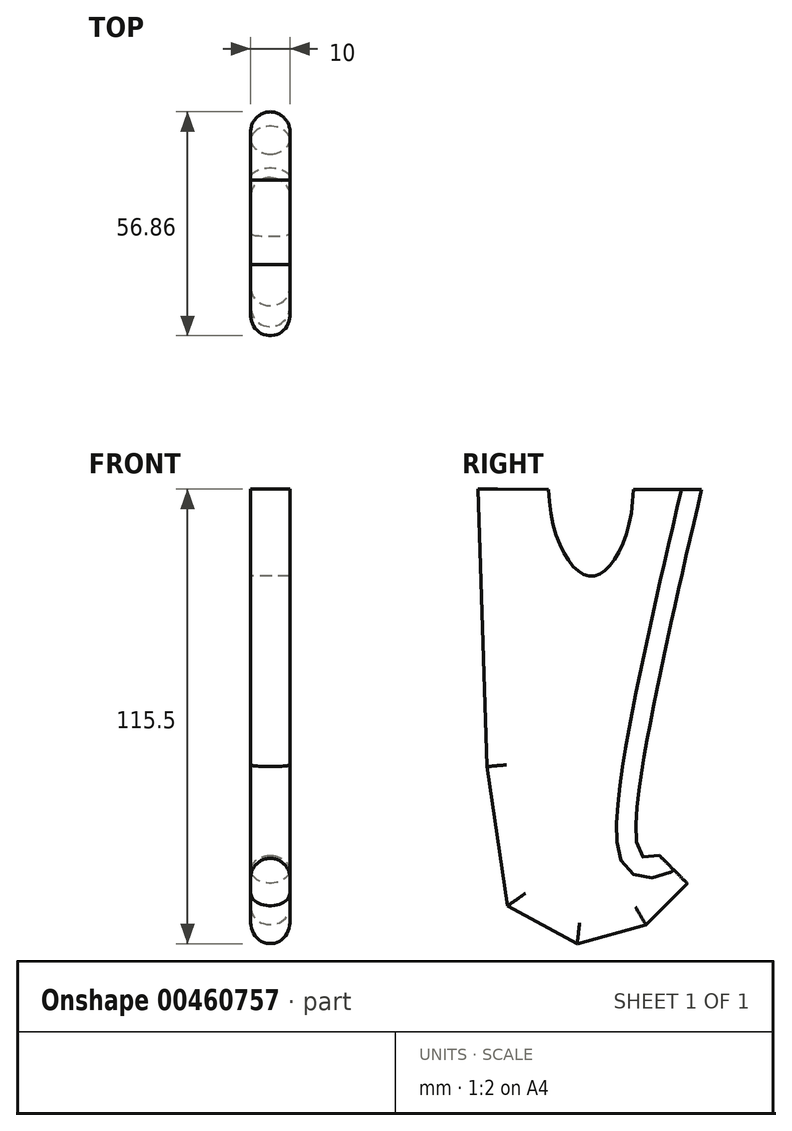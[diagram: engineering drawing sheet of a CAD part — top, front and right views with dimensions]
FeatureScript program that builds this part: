
annotation { "Feature Type Name" : "Feature", "Feature Type Description" : "" }
export const myFeature = defineFeature(function(context is Context, id is Id, definition is map)
    precondition{}
    {
        {
            var Q0;
            Q0=qCreatedBy(makeId("Top.planeOp"),FACE);
            var sketch = newSketch(context, id + "F0", { "sketchPlane" : qUnion([Q0])});
            skLineSegment(sketch, "E0.bottom", {"start": v(50, 50) * mm, "end": v(-50, 50) * mm});
            skLineSegment(sketch, "E0.top", {"start": v(50, -50) * mm, "end": v(-50, -50) * mm});
            skLineSegment(sketch, "E0.left", {"start": v(50, 50) * mm, "end": v(50, -50) * mm});
            skLineSegment(sketch, "E0.right", {"start": v(-50, 50) * mm, "end": v(-50, -50) * mm});
            skPoint(sketch, "E0.middle", {"position": v(0, 0) * mm});
            skSolve(sketch);
        }
        {
            var Q0;
            Q0=qCreatedBy(makeId("Right.planeOp"),FACE);
            var sketch = newSketch(context, id + "F1", { "sketchPlane" : qUnion([Q0])});
            skLineSegment(sketch, "E1", {"start": v(32.93, -92.93) * mm, "end": v(40, -100) * mm});
            skLineSegment(sketch, "E2", {"start": v(40, -100) * mm, "end": v(50, -100) * mm});
            skLineSegment(sketch, "E3", {"start": v(50, -100) * mm, "end": v(50, 0) * mm});
            skLineSegment(sketch, "E4", {"start": v(40, -100) * mm, "end": v(29.49, -110.51) * mm});
            skLineSegment(sketch, "E5", {"start": v(29.49, -110.51) * mm, "end": v(12.06, -115.35) * mm});
            skLineSegment(sketch, "E6", {"start": v(12.06, -115.35) * mm, "end": v(-5.63, -105.7) * mm});
            skLineSegment(sketch, "E7", {"start": v(-5.63, -105.7) * mm, "end": v(-10.9, -70.34) * mm});
            skLineSegment(sketch, "E8", {"start": v(-10.9, -70.34) * mm, "end": v(-13.2, 0.15) * mm});
            skFitSpline(sketch, "E9", {"points": [v(32.93, -92.93) * mm, v(28.21, -92.93) * mm, v(43.66, 0.05) * mm], "startDerivative": vector(-29.89, -10.4) * mm, "endDerivative": vector(37.17, 160.27) * mm});
            skLineSegment(sketch, "E10", {"start": v(43.66, 0.05) * mm, "end": v(-13.2, 0.15) * mm});
            skFitSpline(sketch, "E11", {"points": [v(26.3, 0.08) * mm, v(15.78, -21.95) * mm, v(4.81, 0.12) * mm], "startDerivative": vector(-1.32, -70.5) * mm, "endDerivative": vector(-1.3, 73.03) * mm});
            skSolve(sketch);
        }
        {
            var Q0;
            Q0=makeQuery(id+"F1.imprint","IMPRINT",FACE,{"disambiguationData":[TD([[makeQuery(id+"F1.imprint","IMPRINT",EDGE,{"derivedFrom":sQuery(id+"F1.wireOp",EDGE,"E1")}),-1.0]])]});
            extrude(context, id + "F2", {"entities" : qUnion([Q0]), "endBound" : BoundingType.SYMMETRIC, "depth" : 10 * mm});
        }
        {
            var Q0;
            Q0=makeQuery(id+"F2.opExtrude","CAP_EDGE",EDGE,{"disambiguationData":[OSD([sQuery(id+"F1.wireOp",EDGE,"E9")])],"isStart":false});
            var Q1;
            Q1=makeQuery(id+"F2.opExtrude","CAP_EDGE",EDGE,{"disambiguationData":[OSD([sQuery(id+"F1.wireOp",EDGE,"E4")])],"isStart":false});
            var Q2;
            Q2=makeQuery(id+"F2.opExtrude","CAP_EDGE",EDGE,{"disambiguationData":[OSD([sQuery(id+"F1.wireOp",EDGE,"E5")])],"isStart":false});
            var Q3;
            Q3=makeQuery(id+"F2.opExtrude","CAP_EDGE",EDGE,{"disambiguationData":[OSD([sQuery(id+"F1.wireOp",EDGE,"E6")])],"isStart":false});
            var Q4;
            Q4=makeQuery(id+"F2.opExtrude","CAP_EDGE",EDGE,{"disambiguationData":[OSD([sQuery(id+"F1.wireOp",EDGE,"E7")])],"isStart":false});
            var Q5;
            Q5=makeQuery(id+"F2.opExtrude","CAP_EDGE",EDGE,{"disambiguationData":[OSD([sQuery(id+"F1.wireOp",EDGE,"E8")])],"isStart":false});
            var Q6;
            Q6=makeQuery(id+"F2.opExtrude","CAP_EDGE",EDGE,{"disambiguationData":[OSD([sQuery(id+"F1.wireOp",EDGE,"E9")])],"isStart":true});
            var Q7;
            Q7=makeQuery(id+"F2.opExtrude","CAP_EDGE",EDGE,{"disambiguationData":[OSD([sQuery(id+"F1.wireOp",EDGE,"E4")])],"isStart":true});
            var Q8;
            Q8=makeQuery(id+"F2.opExtrude","CAP_EDGE",EDGE,{"disambiguationData":[OSD([sQuery(id+"F1.wireOp",EDGE,"E5")])],"isStart":true});
            var Q9;
            Q9=makeQuery(id+"F2.opExtrude","CAP_EDGE",EDGE,{"disambiguationData":[OSD([sQuery(id+"F1.wireOp",EDGE,"E6")])],"isStart":true});
            var Q10;
            Q10=makeQuery(id+"F2.opExtrude","CAP_EDGE",EDGE,{"disambiguationData":[OSD([sQuery(id+"F1.wireOp",EDGE,"E7")])],"isStart":true});
            var Q11;
            Q11=makeQuery(id+"F2.opExtrude","CAP_EDGE",EDGE,{"disambiguationData":[OSD([sQuery(id+"F1.wireOp",EDGE,"E8")])],"isStart":true});
            fillet(context, id + "F3", {"entities" : qUnion([Q0, Q1, Q2, Q3, Q4, Q5, Q6, Q7, Q8, Q9, Q10, Q11]), "radius" : 5 * mm, "tangentPropagation" : true, "allowEdgeOverflow" : false});
        }
    });
